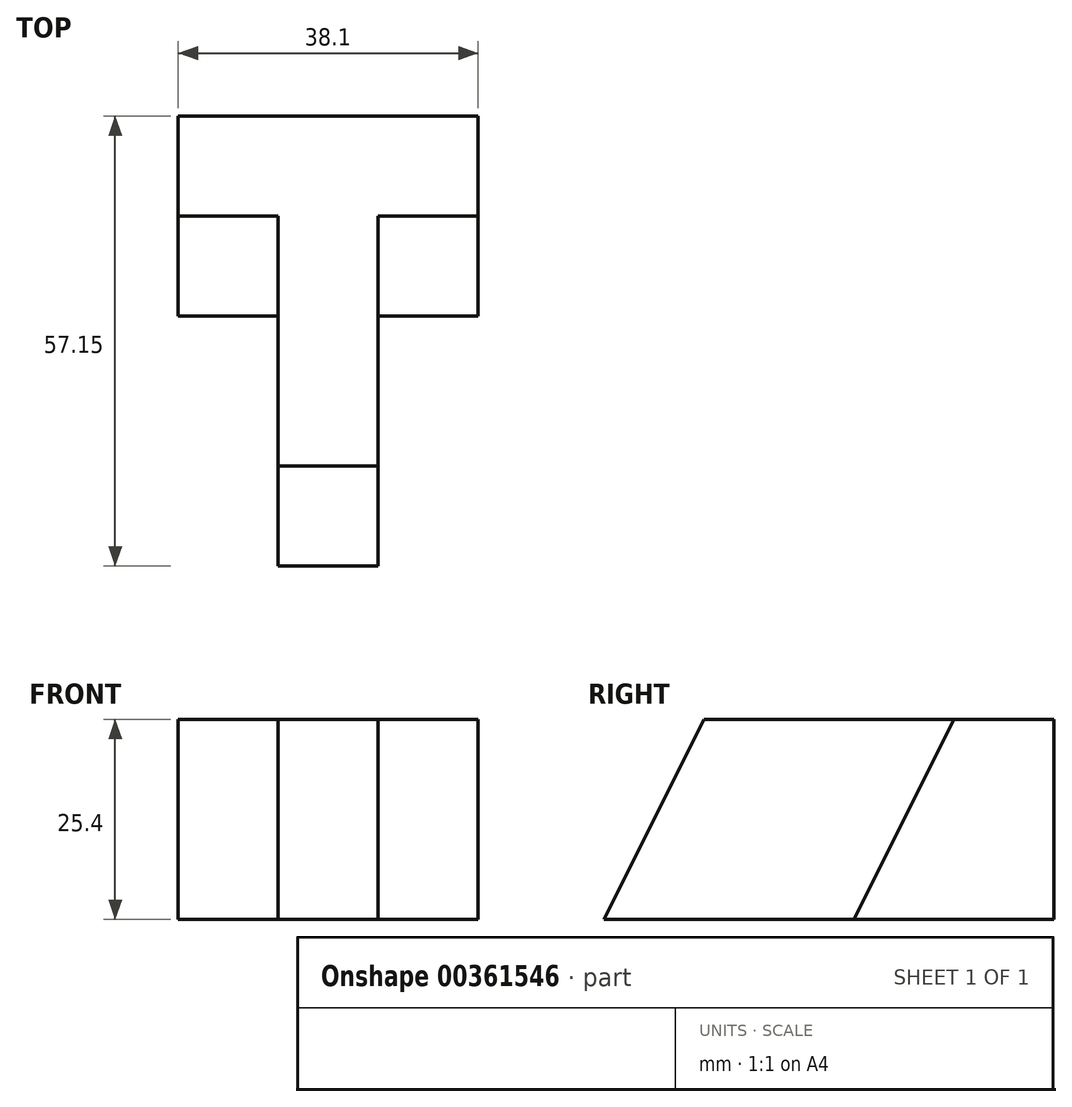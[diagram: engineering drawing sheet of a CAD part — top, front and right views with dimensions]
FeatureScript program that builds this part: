
annotation { "Feature Type Name" : "Feature", "Feature Type Description" : "" }
export const myFeature = defineFeature(function(context is Context, id is Id, definition is map)
    precondition{}
    {
        {
            var Q0;
            Q0=qCreatedBy(makeId("Top.planeOp"),FACE);
            var sketch = newSketch(context, id + "F0", { "sketchPlane" : qUnion([Q0])});
            skLineSegment(sketch, "E0", {"start": v(0, 31.75) * mm, "end": v(0, 0) * mm});
            skLineSegment(sketch, "E1", {"start": v(0, 0) * mm, "end": v(12.7, 0) * mm});
            skLineSegment(sketch, "E2", {"start": v(12.7, 0) * mm, "end": v(12.7, 31.75) * mm});
            skLineSegment(sketch, "E3", {"start": v(0, 31.75) * mm, "end": v(-12.7, 31.75) * mm});
            skLineSegment(sketch, "E4", {"start": v(-12.7, 31.75) * mm, "end": v(-12.7, 57.15) * mm});
            skLineSegment(sketch, "E5", {"start": v(-12.7, 57.15) * mm, "end": v(25.4, 57.15) * mm});
            skLineSegment(sketch, "E6", {"start": v(25.4, 57.15) * mm, "end": v(25.4, 31.75) * mm});
            skLineSegment(sketch, "E7", {"start": v(25.4, 31.75) * mm, "end": v(12.7, 31.75) * mm});
            skSolve(sketch);
        }
        {
            var Q0;
            Q0=makeQuery(id+"F0.imprint","IMPRINT",FACE,{"disambiguationData":[TD([[makeQuery(id+"F0.imprint","IMPRINT",EDGE,{"derivedFrom":sQuery(id+"F0.wireOp",EDGE,"E0")}),1.0]])]});
            extrude(context, id + "F1", {"entities" : qUnion([Q0]), "depth" : 25.4 * mm});
        }
        {
            var Q0;
            Q0=makeQuery(id+"F1.opExtrude","SWEPT_FACE",FACE,{"disambiguationData":[OSD([sQuery(id+"F0.wireOp",EDGE,"E4")])]});
            var sketch = newSketch(context, id + "F2", { "sketchPlane" : qUnion([Q0])});
            skLineSegment(sketch, "E8", {"start": v(-44.45, 25.4) * mm, "end": v(-31.75, 0) * mm});
            skLineSegment(sketch, "E9", {"start": v(-44.45, 25.4) * mm, "end": v(-31.75, 25.4) * mm});
            skLineSegment(sketch, "E10", {"start": v(-31.75, 25.4) * mm, "end": v(-31.75, 0) * mm});
            skSolve(sketch);
        }
        {
            var Q0;
            Q0 = qSketchRegion(id + "F2", true);
            extrude(context, id + "F3", {"entities" : qUnion([Q0]), "operationType" : NewBodyOperationType.REMOVE, "oppositeDirection" : true, "depth" : 12.7 * mm});
        }
        {
            var Q0;
            Q0=makeQuery(id+"F1.opExtrude","SWEPT_FACE",FACE,{"disambiguationData":[OSD([sQuery(id+"F0.wireOp",EDGE,"E6")])]});
            var sketch = newSketch(context, id + "F4", { "sketchPlane" : qUnion([Q0])});
            skLineSegment(sketch, "E11", {"start": v(44.45, 25.4) * mm, "end": v(31.75, 0) * mm});
            skLineSegment(sketch, "E12", {"start": v(31.75, 0) * mm, "end": v(31.75, 25.4) * mm});
            skLineSegment(sketch, "E13", {"start": v(31.75, 25.4) * mm, "end": v(44.45, 25.4) * mm});
            skSolve(sketch);
        }
        {
            var Q0;
            Q0 = qSketchRegion(id + "F4", true);
            extrude(context, id + "F5", {"entities" : qUnion([Q0]), "operationType" : NewBodyOperationType.REMOVE, "oppositeDirection" : true, "depth" : 12.7 * mm});
        }
        {
            var Q0;
            Q0=makeQuery(id+"F3.boolean.opBoolean","MERGE",FACE,{"derivedFrom":[makeQuery(id+"F1.opExtrude","SWEPT_FACE",FACE,{"disambiguationData":[OSD([sQuery(id+"F0.wireOp",EDGE,"E0")])]}),makeQuery(id+"F3.opExtrude","CAP_FACE",FACE,{"disambiguationData":[OSD([sQuery(id+"F2.wireOp",EDGE,"E8"),sQuery(id+"F2.wireOp",EDGE,"E9"),sQuery(id+"F2.wireOp",EDGE,"E10")])],"isStart":false})]});
            var sketch = newSketch(context, id + "F6", { "sketchPlane" : qUnion([Q0])});
            skLineSegment(sketch, "E14", {"start": v(-12.7, 25.4) * mm, "end": v(0, 0) * mm});
            skLineSegment(sketch, "E15", {"start": v(0, 0) * mm, "end": v(0, 25.4) * mm});
            skLineSegment(sketch, "E16", {"start": v(0, 25.4) * mm, "end": v(-12.7, 25.4) * mm});
            skSolve(sketch);
        }
        {
            var Q0;
            Q0 = qSketchRegion(id + "F6", true);
            extrude(context, id + "F7", {"entities" : qUnion([Q0]), "operationType" : NewBodyOperationType.REMOVE, "oppositeDirection" : true, "depth" : 12.7 * mm});
        }
    });
